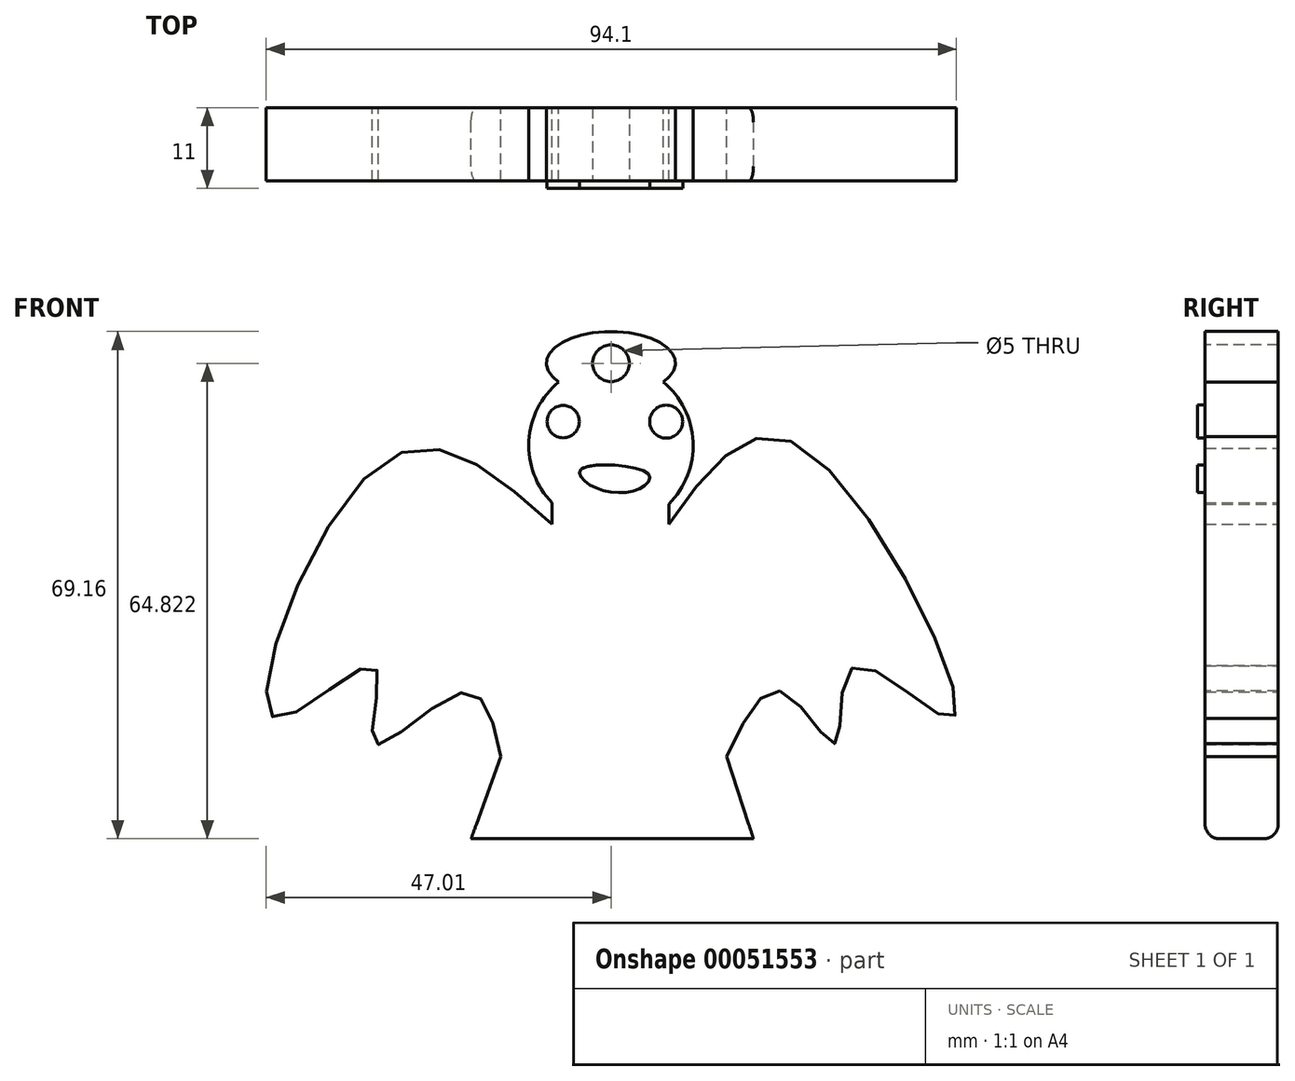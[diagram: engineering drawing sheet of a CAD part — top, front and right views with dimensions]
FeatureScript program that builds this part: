
annotation { "Feature Type Name" : "Feature", "Feature Type Description" : "" }
export const myFeature = defineFeature(function(context is Context, id is Id, definition is map)
    precondition{}
    {
        {
            var Q0;
            Q0=qCreatedBy(makeId("Front.planeOp"),FACE);
            var sketch = newSketch(context, id + "F0", { "sketchPlane" : qUnion([Q0])});
            skArc(sketch, "E0", {"start": v(7.88, -7.97) * mm, "mid": v(0.1, 11.21) * mm, "end": v(-8.03, -7.82) * mm});
            skLineSegment(sketch, "E1", {"start": v(-8.03, -7.82) * mm, "end": v(-8.03, -10.72) * mm});
            skLineSegment(sketch, "E2", {"start": v(7.88, -7.97) * mm, "end": v(7.88, -10.72) * mm});
            skFitSpline(sketch, "E3", {"points": [v(-8.03, -10.72) * mm, v(-31.34, -2.47) * mm, v(-45.82, -37.12) * mm, v(-32.26, -30.15) * mm, v(-32.26, -40.6) * mm, v(-20.16, -33.64) * mm, v(-15.03, -42.43) * mm], "startDerivative": vector(-118.1, 105.74) * mm, "endDerivative": vector(22.5, -110.48) * mm});
            skLineSegment(sketch, "E4", {"start": v(-15.03, -42.43) * mm, "end": v(-19.06, -53.61) * mm});
            skLineSegment(sketch, "E5", {"start": v(-19.06, -53.61) * mm, "end": v(19.43, -53.61) * mm});
            skFitSpline(sketch, "E6", {"points": [v(7.88, -10.72) * mm, v(25.66, 0) * mm, v(46.56, -37.12) * mm, v(33.18, -30.15) * mm, v(30.61, -40.6) * mm, v(23.46, -33.64) * mm, v(15.76, -42.43) * mm], "startDerivative": vector(86.72, 121.56) * mm, "endDerivative": vector(-51.42, -109.53) * mm});
            skLineSegment(sketch, "E7", {"start": v(15.76, -42.43) * mm, "end": v(19.43, -53.61) * mm});
            skEllipse(sketch, "E8", {"center": v(0, 11.21) * mm, "majorRadius": 8.8 * mm, "minorRadius": 4.34 * mm, "majorAxis": v(-1, 0)});
            skSolve(sketch);
        }
        {
            var Q0;
            {var subQ1=sQuery(id+"F0.wireOp",EDGE,"E1");Q0=makeQuery(id+"F0.imprint","IMPRINT",FACE,{"disambiguationData":[TD([[makeQuery(id+"F0.imprint","IMPRINT",EDGE,{"derivedFrom":subQ1}),1.0]])]});}
            var Q1;
            {var subQ0=sQuery(id+"F0.wireOp",EDGE,"E8");var subQ1=sQuery(id+"F0.wireOp",EDGE,"E0");var subQ2=makeQuery(id+"F0.imprint","INTERSECT",VERTEX,{"disambiguationData":[OD(0.0)],"derivedFrom":[subQ1,subQ0]});Q1=makeQuery(id+"F0.imprint","IMPRINT",FACE,{"disambiguationData":[TD([[makeQuery(id+"F0.imprint","IMPRINT",EDGE,{"disambiguationData":[TD([[subQ2,-1.0]])],"derivedFrom":subQ1}),1.0]])]});}
            var Q2;
            {var subQ0=sQuery(id+"F0.wireOp",EDGE,"E8");var subQ1=sQuery(id+"F0.wireOp",EDGE,"E0");var subQ2=makeQuery(id+"F0.imprint","INTERSECT",VERTEX,{"disambiguationData":[OD(0.0)],"derivedFrom":[subQ1,subQ0]});Q2=makeQuery(id+"F0.imprint","IMPRINT",FACE,{"disambiguationData":[TD([[makeQuery(id+"F0.imprint","IMPRINT",EDGE,{"disambiguationData":[TD([[subQ2,-1.0]])],"derivedFrom":subQ1}),-1.0]])]});}
            extrude(context, id + "F1", {"entities" : qUnion([Q0, Q1, Q2]), "depth" : 10 * mm});
        }
        {
            var Q0;
            Q0=makeQuery(id+"F1.opExtrude","CAP_FACE",FACE,{"disambiguationData":[OSD([sQuery(id+"F0.wireOp",EDGE,"E0"),sQuery(id+"F0.wireOp",EDGE,"E1"),sQuery(id+"F0.wireOp",EDGE,"E2"),sQuery(id+"F0.wireOp",EDGE,"E3"),sQuery(id+"F0.wireOp",EDGE,"E4"),sQuery(id+"F0.wireOp",EDGE,"E5"),sQuery(id+"F0.wireOp",EDGE,"E6"),sQuery(id+"F0.wireOp",EDGE,"E7"),sQuery(id+"F0.wireOp",EDGE,"E8")])],"isStart":false});
            var sketch = newSketch(context, id + "F2", { "sketchPlane" : qUnion([Q0])});
            skEllipse(sketch, "E9", {"center": v(0, 11.21) * mm, "majorRadius": 8.82 * mm, "minorRadius": 4.32 * mm, "majorAxis": v(-1, 0)});
            skSolve(sketch);
        }
        {
            var Q0;
            Q0=sQuery(id+"F2.wireOp",VERTEX,"E9.center");
            var Q1;
            Q1=makeQuery(id+"F1.opExtrude","SWEPT_BODY",BODY,{"disambiguationData":[OSD([sQuery(id+"F0.wireOp",EDGE,"E0"),sQuery(id+"F0.wireOp",EDGE,"E1"),sQuery(id+"F0.wireOp",EDGE,"E2"),sQuery(id+"F0.wireOp",EDGE,"E3"),sQuery(id+"F0.wireOp",EDGE,"E4"),sQuery(id+"F0.wireOp",EDGE,"E5"),sQuery(id+"F0.wireOp",EDGE,"E6"),sQuery(id+"F0.wireOp",EDGE,"E7"),sQuery(id+"F0.wireOp",EDGE,"E8")])]});
            hole(context, id + "F3", {"style" : HoleStyle.SIMPLE, "holeDiameter" : 5 * mm, "endStyle" : HoleEndStyle.THROUGH, "locations" : qUnion([Q0]), "scope" : qUnion([Q1])});
        }
        {
            var Q0;
            Q0=makeQuery(id+"F1.opExtrude","CAP_EDGE",EDGE,{"disambiguationData":[OSD([sQuery(id+"F0.wireOp",EDGE,"E5")])],"isStart":false});
            var Q1;
            Q1=makeQuery(id+"F1.opExtrude","CAP_EDGE",EDGE,{"disambiguationData":[OSD([sQuery(id+"F0.wireOp",EDGE,"E5")])],"isStart":true});
            fillet(context, id + "F4", {"entities" : qUnion([Q0, Q1]), "radius" : 2 * mm, "tangentPropagation" : true, "allowEdgeOverflow" : false});
        }
        {
            var Q0;
            Q0=makeQuery(id+"F1.opExtrude","CAP_FACE",FACE,{"disambiguationData":[OSD([sQuery(id+"F0.wireOp",EDGE,"E0"),sQuery(id+"F0.wireOp",EDGE,"E1"),sQuery(id+"F0.wireOp",EDGE,"E2"),sQuery(id+"F0.wireOp",EDGE,"E3"),sQuery(id+"F0.wireOp",EDGE,"E4"),sQuery(id+"F0.wireOp",EDGE,"E5"),sQuery(id+"F0.wireOp",EDGE,"E6"),sQuery(id+"F0.wireOp",EDGE,"E7"),sQuery(id+"F0.wireOp",EDGE,"E8")])],"isStart":false});
            var sketch = newSketch(context, id + "F5", { "sketchPlane" : qUnion([Q0])});
            skCircle(sketch, "E10", {"center": v(-6.51, 3.26) * mm, "radius": 2.2 * mm});
            skCircle(sketch, "E11", {"center": v(7.53, 3.26) * mm, "radius": 2.25 * mm});
            skFitSpline(sketch, "E12", {"points": [v(-4.07, -3.26) * mm, v(-2.65, -5.5) * mm, v(3.87, -5.9) * mm, v(5.09, -3.87) * mm, v(-4.07, -3.26) * mm]});
            skSolve(sketch);
        }
        {
            var Q0;
            Q0=makeQuery(id+"F5.imprint","IMPRINT",FACE,{"disambiguationData":[TD([[makeQuery(id+"F5.imprint","IMPRINT",EDGE,{"derivedFrom":sQuery(id+"F5.wireOp",EDGE,"E10")}),1.0]])]});
            var Q1;
            Q1=makeQuery(id+"F5.imprint","IMPRINT",FACE,{"disambiguationData":[TD([[makeQuery(id+"F5.imprint","IMPRINT",EDGE,{"derivedFrom":sQuery(id+"F5.wireOp",EDGE,"E11")}),1.0]])]});
            var Q2;
            Q2=makeQuery(id+"F5.imprint","IMPRINT",FACE,{"disambiguationData":[TD([[makeQuery(id+"F5.imprint","IMPRINT",EDGE,{"derivedFrom":sQuery(id+"F5.wireOp",EDGE,"E12")}),1.0]])]});
            extrude(context, id + "F6", {"entities" : qUnion([Q0, Q1, Q2]), "operationType" : NewBodyOperationType.ADD, "depth" : 1 * mm});
        }
    });
